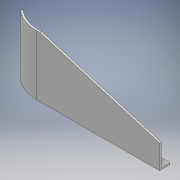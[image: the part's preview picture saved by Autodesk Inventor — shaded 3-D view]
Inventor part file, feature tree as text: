
AUTODESK INVENTOR PART (.ipt)
format: ipt  version: 2018 (Build 220112000, 112)  size: 169,472 bytes
history: native  units: mm
features: extrude x6, sketch x6, other x1
ambient origin geometry x8: Origin, YZ Plane, XZ Plane, XY Plane, X Axis, Y Axis, Z Axis, Center Point
bodies: Body1 (feature_tree)
feature tree (13):
  extrude  "押し出し1"  Depth=250.0mm
  extrude  "押し出し2"  Depth=500.0mm
  extrude  "押し出し5"  Depth=100.0mm
  extrude  "押し出し7"  Depth=200.0mm
  other  "面を削除1"
  extrude  "押し出し9"  Depth=35.0mm TaperAngle=0.0deg
  extrude  "押し出し10"  Depth=90.0mm
  sketch  "スケッチ1"
  sketch  "スケッチ2"
  sketch  "スケッチ5"
  sketch  "スケッチ8"
  sketch  "スケッチ10"
  sketch  "スケッチ11"
